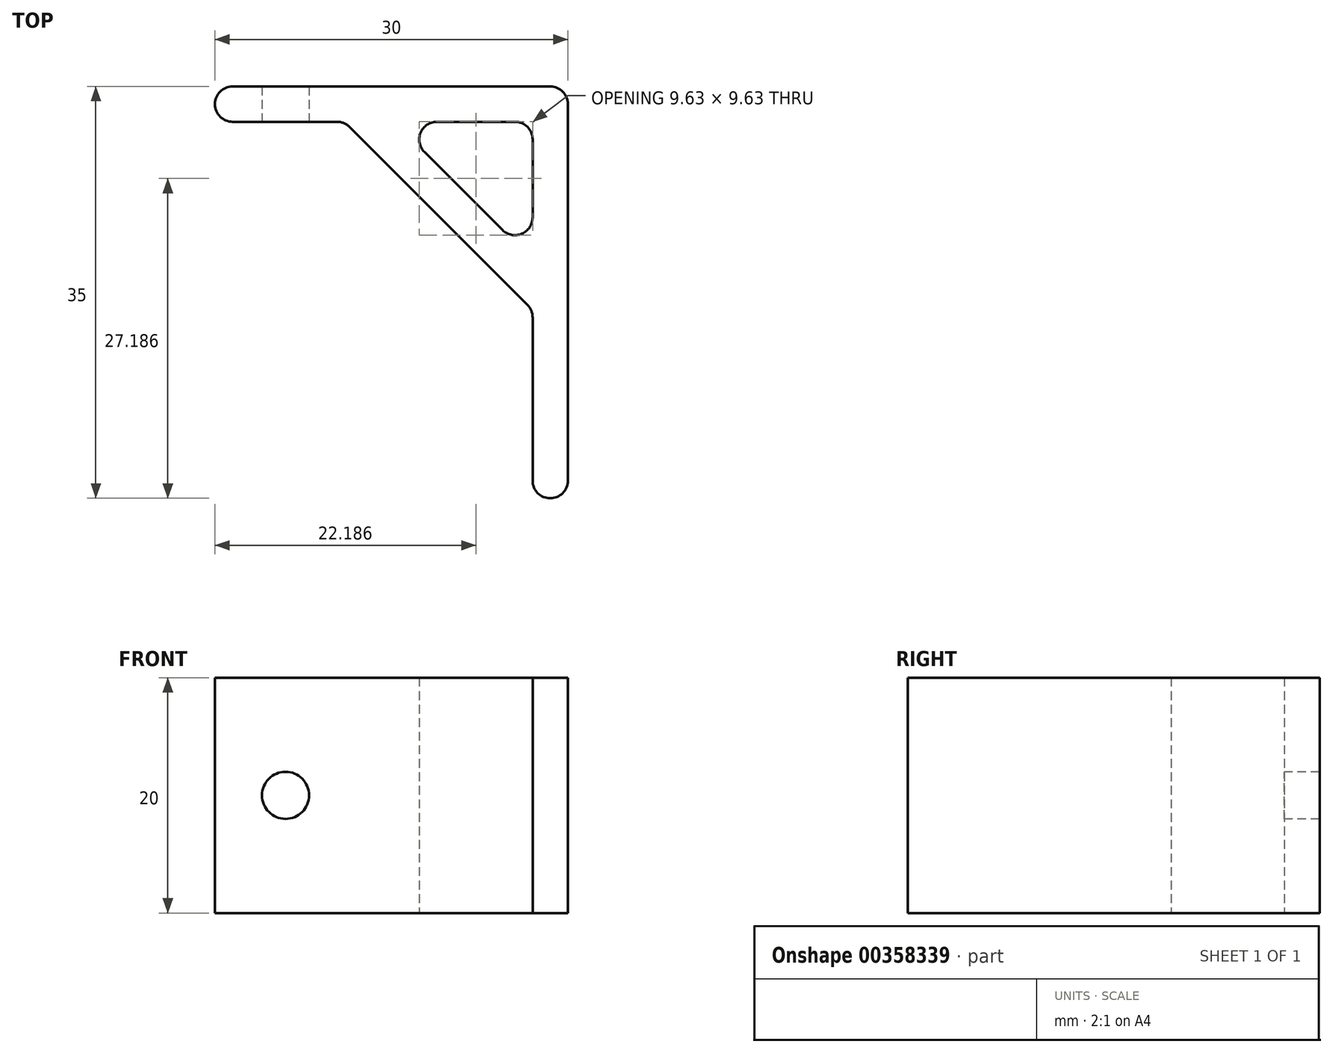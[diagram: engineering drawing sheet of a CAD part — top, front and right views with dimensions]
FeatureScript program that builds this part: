
annotation { "Feature Type Name" : "Feature", "Feature Type Description" : "" }
export const myFeature = defineFeature(function(context is Context, id is Id, definition is map)
    precondition{}
    {
        {
            var Q0;
            Q0=qCreatedBy(makeId("Top.planeOp"),FACE);
            var sketch = newSketch(context, id + "F0", { "sketchPlane" : qUnion([Q0])});
            skLineSegment(sketch, "E0", {"start": v(-19, 11) * mm, "end": v(11, 11) * mm});
            skLineSegment(sketch, "E1", {"start": v(11, 11) * mm, "end": v(11, -24) * mm});
            skLineSegment(sketch, "E2", {"start": v(11, -24) * mm, "end": v(8, -24) * mm});
            skLineSegment(sketch, "E3", {"start": v(8, -24) * mm, "end": v(8, 8) * mm});
            skLineSegment(sketch, "E4", {"start": v(8, 8) * mm, "end": v(-19, 8) * mm});
            skLineSegment(sketch, "E5", {"start": v(-19, 8) * mm, "end": v(-19, 11) * mm});
            skLineSegment(sketch, "E6", {"start": v(-8, 8) * mm, "end": v(8, -8) * mm});
            skLineSegment(sketch, "E7", {"start": v(8, -3.76) * mm, "end": v(-3.76, 8) * mm});
            skSolve(sketch);
        }
        {
            var Q0;
            Q0=makeQuery(id+"F0.imprint","IMPRINT",FACE,{"disambiguationData":[TD([[makeQuery(id+"F0.imprint","IMPRINT",EDGE,{"derivedFrom":sQuery(id+"F0.wireOp",EDGE,"E0")}),-1.0]])]});
            var Q1;
            {var subQ0=sQuery(id+"F0.wireOp",EDGE,"E6");Q1=makeQuery(id+"F0.imprint","IMPRINT",FACE,{"disambiguationData":[TD([[makeQuery(id+"F0.imprint","IMPRINT",EDGE,{"derivedFrom":subQ0}),1.0]])]});}
            extrude(context, id + "F1", {"entities" : qUnion([Q0, Q1]), "depth" : 20 * mm});
        }
        {
            var Q0;
            {var subQ0=sQuery(id+"F0.wireOp",EDGE,"E4");Q0=makeQuery(id+"F1.opExtrude","SWEPT_FACE",FACE,{"disambiguationData":[OSD([subQ0]),TDD([makeQuery(id+"F0.imprint","IMPRINT",EDGE,{"disambiguationData":[TD([[makeQuery(id+"F0.imprint","INTERSECT",VERTEX,{"derivedFrom":[subQ0,sQuery(id+"F0.wireOp",EDGE,"E5")]}),1.0]])],"derivedFrom":subQ0})])]});}
            var sketch = newSketch(context, id + "F2", { "sketchPlane" : qUnion([Q0])});
            skCircle(sketch, "E8", {"center": v(-13, 10) * mm, "radius": 2 * mm});
            skLineSegment(sketch, "E9.0", {"start": v(-19, 20) * mm, "end": v(-19, 0) * mm});
            skLineSegment(sketch, "E10", {"start": v(-19, 10) * mm, "end": v(-13, 10) * mm, "construction": true});
            skSolve(sketch);
        }
        {
            var Q0;
            Q0=makeQuery(id+"F1.opExtrude","SWEPT_EDGE",EDGE,{"disambiguationData":[OSD([sQuery(id+"F0.wireOp",EDGE,"E4"),sQuery(id+"F0.wireOp",EDGE,"E5")])]});
            var Q1;
            Q1=makeQuery(id+"F1.opExtrude","SWEPT_EDGE",EDGE,{"disambiguationData":[OSD([sQuery(id+"F0.wireOp",EDGE,"E0"),sQuery(id+"F0.wireOp",EDGE,"E5")])]});
            var Q2;
            Q2=makeQuery(id+"F1.opExtrude","SWEPT_EDGE",EDGE,{"disambiguationData":[OSD([sQuery(id+"F0.wireOp",EDGE,"E4"),sQuery(id+"F0.wireOp",EDGE,"E6")])]});
            var Q3;
            Q3=makeQuery(id+"F1.opExtrude","SWEPT_EDGE",EDGE,{"disambiguationData":[OSD([sQuery(id+"F0.wireOp",EDGE,"E2"),sQuery(id+"F0.wireOp",EDGE,"E3")])]});
            var Q4;
            Q4=makeQuery(id+"F1.opExtrude","SWEPT_EDGE",EDGE,{"disambiguationData":[OSD([sQuery(id+"F0.wireOp",EDGE,"E1"),sQuery(id+"F0.wireOp",EDGE,"E2")])]});
            var Q5;
            Q5=makeQuery(id+"F1.opExtrude","SWEPT_EDGE",EDGE,{"disambiguationData":[OSD([sQuery(id+"F0.wireOp",EDGE,"E3"),sQuery(id+"F0.wireOp",EDGE,"E6")])]});
            var Q6;
            Q6=makeQuery(id+"F1.opExtrude","SWEPT_EDGE",EDGE,{"disambiguationData":[OSD([sQuery(id+"F0.wireOp",EDGE,"E3"),sQuery(id+"F0.wireOp",EDGE,"E4")])]});
            var Q7;
            Q7=makeQuery(id+"F1.opExtrude","SWEPT_EDGE",EDGE,{"disambiguationData":[OSD([sQuery(id+"F0.wireOp",EDGE,"E0"),sQuery(id+"F0.wireOp",EDGE,"E1")])]});
            var Q8;
            Q8=makeQuery(id+"F1.opExtrude","SWEPT_EDGE",EDGE,{"disambiguationData":[OSD([sQuery(id+"F0.wireOp",EDGE,"E4"),sQuery(id+"F0.wireOp",EDGE,"E7")])]});
            var Q9;
            Q9=makeQuery(id+"F1.opExtrude","SWEPT_EDGE",EDGE,{"disambiguationData":[OSD([sQuery(id+"F0.wireOp",EDGE,"E3"),sQuery(id+"F0.wireOp",EDGE,"E7")])]});
            fillet(context, id + "F3", {"entities" : qUnion([Q0, Q1, Q2, Q3, Q4, Q5, Q6, Q7, Q8, Q9]), "radius" : 1.5 * mm, "tangentPropagation" : true, "allowEdgeOverflow" : false});
        }
        {
            var Q0;
            Q0=makeQuery(id+"F2.imprint","IMPRINT",FACE,{"disambiguationData":[TD([[makeQuery(id+"F2.imprint","IMPRINT",EDGE,{"derivedFrom":sQuery(id+"F2.wireOp",EDGE,"E8")}),1.0]])]});
            var Q1;
            Q1=makeQuery(id+"F1.opExtrude","SWEPT_FACE",FACE,{"disambiguationData":[OSD([sQuery(id+"F0.wireOp",EDGE,"E0")])]});
            extrude(context, id + "F4", {"entities" : qUnion([Q0]), "operationType" : NewBodyOperationType.REMOVE, "endBound" : BoundingType.UP_TO_SURFACE, "oppositeDirection" : true, "endBoundEntityFace" : qUnion([Q1]), "depth" : 25 * mm});
        }
    });
